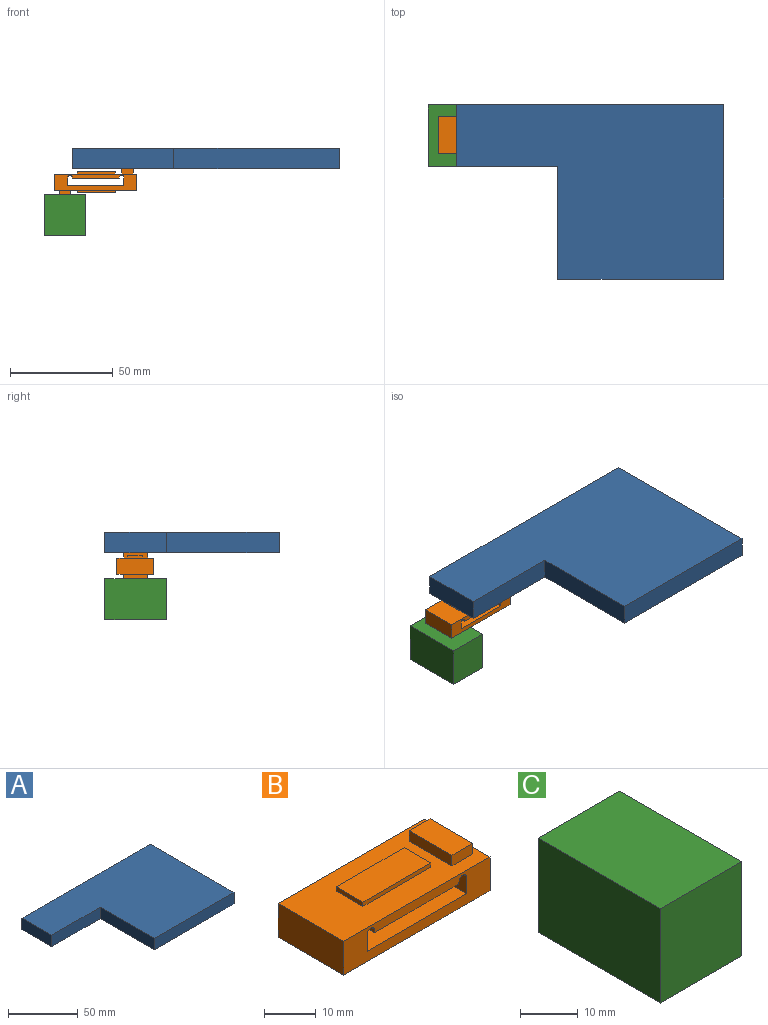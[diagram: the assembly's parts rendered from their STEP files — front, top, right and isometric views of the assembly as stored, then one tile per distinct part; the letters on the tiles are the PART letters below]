
ASSEMBLY  parts=3 mates=2
PART A: 8 faces, bbox 130x84.9x10 mm
  f0: plane 49.29x10mm, normal (0,-1,0), area 492.9mm2, adj f1,f5,f6,f7
  f1: plane 54.94x10mm, normal (-1,0,0), area 549.4mm2, adj f0,f2,f6,f7
  f2: plane 80.71x10mm, normal (0,-1,0), area 807.1mm2, adj f1,f3,f6,f7
  f3: plane 84.94x10mm, normal (1,0,0), area 849.4mm2, adj f2,f4,f6,f7
  f4: plane 130x10mm, normal (0,1,0), area 1300mm2, adj f3,f5,f6,f7
  f5: plane 30x10mm, normal (-1,0,0), area 300mm2, adj f0,f4,f6,f7
  f6: plane 130x84.94mm, normal (0,0,1), area 8334mm2, adj f0,f1,f2,f3,f4,f5
  f7: plane 130x84.94mm, normal (0,0,-1), area 8334mm2, adj f0,f1,f2,f3,f4,f5
PART B: 39 faces, bbox 40x18x12.5 mm
  f0: plane 40x8mm, normal (0,-1,0), area 223.2mm2, adj f2,f3,f4,f5,f16,f17,f18,f19
  f1: plane 40x8mm, normal (0,1,0), area 223.2mm2, adj f2,f3,f4,f5,f16,f17,f18,f19
  f2: plane 40x18mm, normal (0,0,-1), area 516.4mm2, adj f0,f1,f3,f4,f11,f12,f13,f14
  f3: plane 18x8mm, normal (-1,0,0), area 144mm2, adj f0,f1,f2,f5
  f4: plane 18x8mm, normal (1,0,0), area 144mm2, adj f0,f1,f2,f5
  f5: plane 40x18mm, normal (0,0,1), area 518.7mm2, adj f0,f1,f3,f4,f6,f7,f8,f9
  f6: plane 7.29x1mm, normal (-1,0,0), area 7.3mm2, adj f5,f7,f9,f10
  f7: plane 18.6x1mm, normal (0,-1,0), area 18.6mm2, adj f5,f6,f8,f10
  f8: plane 7.29x1mm, normal (1,0,0), area 7.3mm2, adj f5,f7,f9,f10
  f9: plane 18.6x1mm, normal (0,1,0), area 18.6mm2, adj f5,f6,f8,f10
  f10: plane 18.6x7.29mm, normal (0,0,1), area 135.6mm2, adj f6,f7,f8,f9
  f11: plane 7.29x1mm, normal (-1,0,0), area 7.3mm2, adj f2,f12,f14,f15
  f12: plane 18.6x1mm, normal (0,-1,0), area 18.6mm2, adj f2,f11,f13,f15
  f13: plane 7.29x1mm, normal (1,0,0), area 7.3mm2, adj f2,f12,f14,f15
  f14: plane 18.6x1mm, normal (0,1,0), area 18.6mm2, adj f2,f11,f13,f15
  f15: plane 18.6x7.29mm, normal (0,0,-1), area 135.6mm2, adj f11,f12,f13,f14
  f16: plane 18x4.06mm, normal (1,0,0), area 73.2mm2, adj f0,f1,f22,f27
  f17: plane 18x4.06mm, normal (-1,0,0), area 73.2mm2, adj f0,f1,f18,f27
  f18: cylinder r=1.11mm len=18mm, axis (0,-1,0), area 53mm2, adj f0,f1,f17,f19
  f19: plane 18x0.73mm, normal (1,0,0), area 13.2mm2, adj f0,f1,f18,f20
  f20: plane 23x18mm, normal (0,0,-1), area 414mm2, adj f0,f1,f19,f21
  f21: plane 18x0.73mm, normal (-1,0,0), area 13.2mm2, adj f0,f1,f20,f22
  f22: cylinder r=1.11mm len=18mm, axis (0,-1,0), area 53mm2, adj f0,f1,f16,f21
  f23: plane 7.29x0.38mm, normal (1,0,0), area 2.8mm2, adj f24,f26,f27,f28
  f24: plane 18.6x0.38mm, normal (0,1,0), area 7.1mm2, adj f23,f25,f27,f28
  f25: plane 7.29x0.38mm, normal (-1,0,0), area 2.8mm2, adj f24,f26,f27,f28
  f26: plane 18.6x0.38mm, normal (0,-1,0), area 7.1mm2, adj f23,f25,f27,f28
  f27: plane 27.3x18mm, normal (0,0,1), area 355.8mm2, adj f0,f1,f16,f17,f23,f24,f25,f26
  f28: plane 18.6x7.29mm, normal (0,0,1), area 135.6mm2, adj f23,f24,f25,f26
  f29: plane 5.65x2.5mm, normal (0,1,0), area 14.1mm2, adj f5,f30,f32,f33
  f30: plane 11.64x2.5mm, normal (-1,0,0), area 29.1mm2, adj f5,f29,f31,f33
  f31: plane 5.65x2.5mm, normal (0,-1,0), area 14.1mm2, adj f5,f30,f32,f33
  f32: plane 11.64x2.5mm, normal (1,0,0), area 29.1mm2, adj f5,f29,f31,f33
  f33: plane 11.64x5.65mm, normal (0,0,1), area 65.7mm2, adj f29,f30,f31,f32
  f34: plane 5.8x2mm, normal (0,-1,0), area 11.6mm2, adj f2,f35,f37,f38
  f35: plane 11.74x2mm, normal (-1,0,0), area 23.5mm2, adj f2,f34,f36,f38
  f36: plane 5.8x2mm, normal (0,1,0), area 11.6mm2, adj f2,f35,f37,f38
  f37: plane 11.74x2mm, normal (1,0,0), area 23.5mm2, adj f2,f34,f36,f38
  f38: plane 11.74x5.8mm, normal (0,0,-1), area 68.1mm2, adj f34,f35,f36,f37
PART C: 6 faces, bbox 20x30x20 mm
  f0: plane 30x20mm, normal (-1,0,0), area 600mm2, adj f1,f3,f4,f5
  f1: plane 20x20mm, normal (0,-1,0), area 400mm2, adj f0,f2,f4,f5
  f2: plane 30x20mm, normal (1,0,0), area 600mm2, adj f1,f3,f4,f5
  f3: plane 20x20mm, normal (0,1,0), area 400mm2, adj f0,f2,f4,f5
  f4: plane 30x20mm, normal (0,0,1), area 600mm2, adj f0,f1,f2,f3
  f5: plane 30x20mm, normal (0,0,-1), area 600mm2, adj f0,f1,f2,f3
PLACE A at identity
PLACE B t=(-8.69,6.07,-10.5)mm
PLACE C t=(-13.68,-0.07,-32.5)mm
MATE fastened A.f7 <-> B.f33  axis (0,0,-1) through (29.65,15,0)mm
MATE fastened B.f38 <-> C.f4  axis (0,0,-1) through (-3.68,14.93,-12.5)mm
